# Revit family: Plum Fix_Basin_Argent_Zen 540 Undercounter
name_source: partatom
category: Plumbing Fixtures
revit_build: Autodesk Revit 2016 (Build: 20190508_0715(x64)
units: mm (PartAtom-declared; Revit-internal decimal feet)

## family parameters
Always vertical = Yes
Cut with Voids When Loaded = Yes
OmniClass Number = 23.45.05.14.14
OmniClass Title = Sinks/Lavatories
Part Type = Normal
Room Calculation Point = No
Round Connector Dimension = Use Diameter
Shared = No
Work Plane-Based = No

## types (1)
- No Tap Hole (FC06TAL00)
    Body Material = z_Argent_Ceramic White
    CW Connection = No
    Cost = 0 $
    Description = Zen 540 Under Counter Basin
    HW Connection = No
    IfcExportAs = IfcSanitaryTerminal
    IfcExportType = WASHHANDBASIN
    Manufacturer = Argent
    Manufacturer_Overall Depth = 353 mm
    Manufacturer_Overall Height = 135 mm
    Manufacturer_Overall Width = 542 mm
    Manufacturer_Spec Code = FC06TAL00
    Manufacturer_URL__Product Specific = https://www.argentaust.com.au
    Model = FC06TAL00
    ModifiedIssue_ANZRS = 20200416 $
    Type Comments = No Tap Hole
    URL = https://www.argentaust.com.au
    Uniclass2015Code = Pr_40_20_96_92
    Uniclass2015Title = Under-mounted washbasins
    Uniclass2015Version = Products v1.17
    Vent Connection = No
    Waste Connection = Yes

## geometry (parser evidence)
native form markers: Sweep x4
no freeform markers — native parametric forms only
